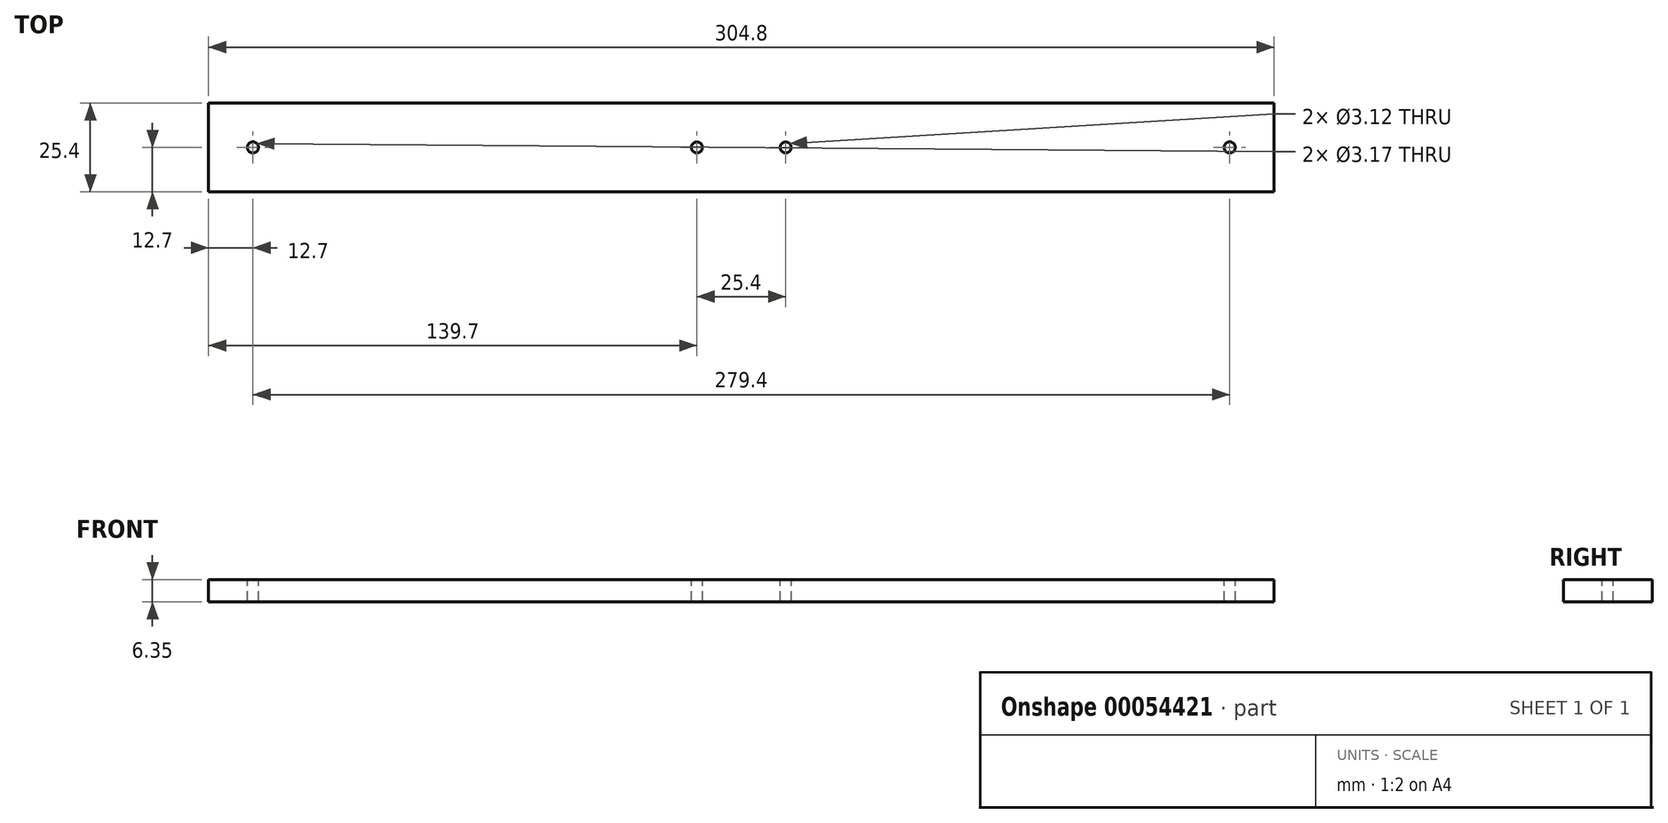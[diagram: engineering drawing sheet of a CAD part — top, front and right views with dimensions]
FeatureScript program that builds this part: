
annotation { "Feature Type Name" : "Feature", "Feature Type Description" : "" }
export const myFeature = defineFeature(function(context is Context, id is Id, definition is map)
    precondition{}
    {
        {
            var Q0;
            Q0=qCreatedBy(makeId("Top.planeOp"),FACE);
            var sketch = newSketch(context, id + "F0", { "sketchPlane" : qUnion([Q0])});
            skLineSegment(sketch, "E0.bottom", {"start": v(0, 0) * mm, "end": v(304.8, 0) * mm});
            skLineSegment(sketch, "E0.top", {"start": v(0, 25.4) * mm, "end": v(304.8, 25.4) * mm});
            skLineSegment(sketch, "E0.left", {"start": v(0, 0) * mm, "end": v(0, 25.4) * mm});
            skLineSegment(sketch, "E0.right", {"start": v(304.8, 0) * mm, "end": v(304.8, 25.4) * mm});
            skSolve(sketch);
        }
        {
            var Q0;
            Q0=makeQuery(id+"F0.imprint","IMPRINT",FACE,{"disambiguationData":[TD([[makeQuery(id+"F0.imprint","IMPRINT",EDGE,{"derivedFrom":sQuery(id+"F0.wireOp",EDGE,"E0.bottom")}),1.0]])]});
            extrude(context, id + "F1", {"entities" : qUnion([Q0]), "depth" : 6.35 * mm});
        }
        {
            var Q0;
            Q0=makeQuery(id+"F1.opExtrude","CAP_FACE",FACE,{"disambiguationData":[OSD([sQuery(id+"F0.wireOp",EDGE,"E0.bottom"),sQuery(id+"F0.wireOp",EDGE,"E0.top"),sQuery(id+"F0.wireOp",EDGE,"E0.left"),sQuery(id+"F0.wireOp",EDGE,"E0.right")])],"isStart":false});
            var sketch = newSketch(context, id + "F2", { "sketchPlane" : qUnion([Q0])});
            skLineSegment(sketch, "E1", {"start": v(152.4, 25.4) * mm, "end": v(152.4, 0) * mm});
            skPoint(sketch, "E2", {"position": v(139.7, 12.7) * mm});
            skPoint(sketch, "E3.MirrorP", {"position": v(165.1, 12.7) * mm});
            skSolve(sketch);
        }
        {
            var Q0;
            Q0=sQuery(id+"F2.wireOp",VERTEX,"E2");
            var Q1;
            Q1=sQuery(id+"F2.wireOp",VERTEX,"E3.MirrorP");
            var Q2;
            Q2=makeQuery(id+"F1.opExtrude","SWEPT_BODY",BODY,{"disambiguationData":[OSD([sQuery(id+"F0.wireOp",EDGE,"E0.bottom"),sQuery(id+"F0.wireOp",EDGE,"E0.top"),sQuery(id+"F0.wireOp",EDGE,"E0.left"),sQuery(id+"F0.wireOp",EDGE,"E0.right")])]});
            hole(context, id + "F3", {"style" : HoleStyle.SIMPLE, "holeDiameter" : 3.12 * mm, "endStyle" : HoleEndStyle.THROUGH, "locations" : qUnion([Q0, Q1]), "scope" : qUnion([Q2])});
        }
        {
            var Q0;
            Q0=makeQuery(id+"F1.opExtrude","CAP_FACE",FACE,{"disambiguationData":[OSD([sQuery(id+"F0.wireOp",EDGE,"E0.bottom"),sQuery(id+"F0.wireOp",EDGE,"E0.top"),sQuery(id+"F0.wireOp",EDGE,"E0.left"),sQuery(id+"F0.wireOp",EDGE,"E0.right")])],"isStart":false});
            var sketch = newSketch(context, id + "F4", { "sketchPlane" : qUnion([Q0])});
            skLineSegment(sketch, "E4", {"start": v(152.4, 25.4) * mm, "end": v(152.4, 0) * mm});
            skPoint(sketch, "E5", {"position": v(12.7, 12.7) * mm});
            skPoint(sketch, "E6.MirrorP", {"position": v(292.1, 12.7) * mm});
            skSolve(sketch);
        }
        {
            var Q0;
            Q0=sQuery(id+"F4.wireOp",VERTEX,"E5");
            var Q1;
            Q1=sQuery(id+"F4.wireOp",VERTEX,"E6.MirrorP");
            var Q2;
            Q2=makeQuery(id+"F1.opExtrude","SWEPT_BODY",BODY,{"disambiguationData":[OSD([sQuery(id+"F0.wireOp",EDGE,"E0.bottom"),sQuery(id+"F0.wireOp",EDGE,"E0.top"),sQuery(id+"F0.wireOp",EDGE,"E0.left"),sQuery(id+"F0.wireOp",EDGE,"E0.right")])]});
            hole(context, id + "F5", {"style" : HoleStyle.SIMPLE, "holeDiameter" : 3.17 * mm, "endStyle" : HoleEndStyle.THROUGH, "locations" : qUnion([Q0, Q1]), "scope" : qUnion([Q2])});
        }
    });
